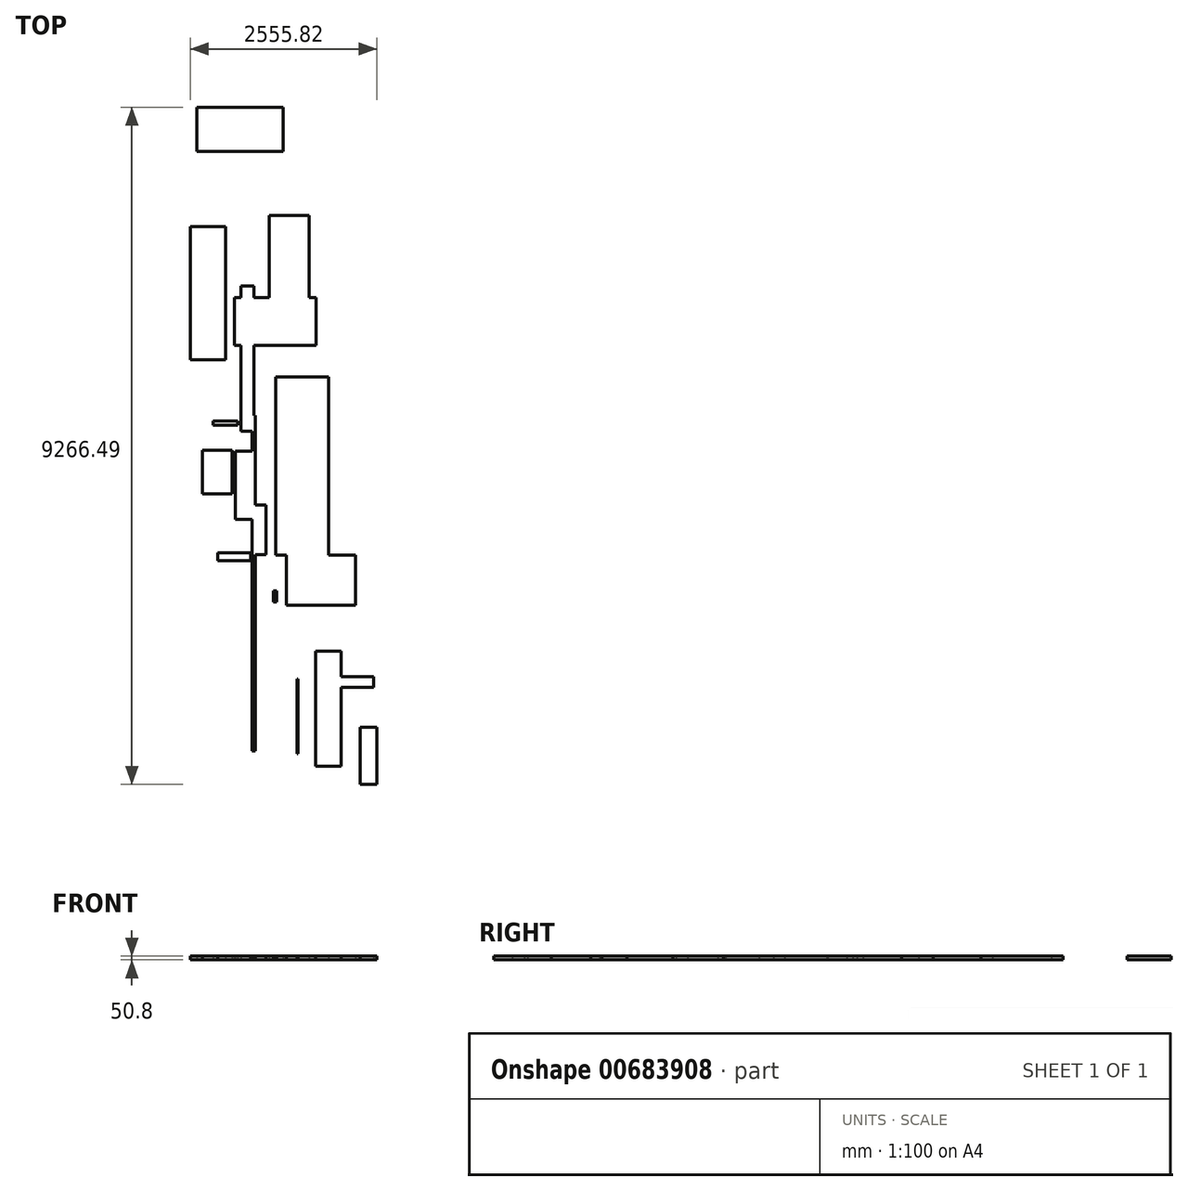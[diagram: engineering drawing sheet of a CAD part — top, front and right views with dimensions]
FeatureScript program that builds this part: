
annotation { "Feature Type Name" : "Feature", "Feature Type Description" : "" }
export const myFeature = defineFeature(function(context is Context, id is Id, definition is map)
    precondition{}
    {
        {
            var Q0;
            Q0=qCreatedBy(makeId("Top.planeOp"),FACE);
            var sketch = newSketch(context, id + "F0", { "sketchPlane" : qUnion([Q0])});
            skLineSegment(sketch, "E0.bottom", {"start": v(975.33, -2927.2) * mm, "end": v(1019.57, -2927.2) * mm});
            skLineSegment(sketch, "E0.top", {"start": v(975.33, -3083.63) * mm, "end": v(1019.57, -3083.63) * mm});
            skLineSegment(sketch, "E0.left", {"start": v(975.33, -2927.2) * mm, "end": v(975.33, -3083.63) * mm});
            skLineSegment(sketch, "E0.right", {"start": v(1019.57, -2927.2) * mm, "end": v(1019.57, -3083.63) * mm});
            skLineSegment(sketch, "E1.bottom", {"start": v(686.68, -1751.09) * mm, "end": v(872.32, -1751.09) * mm});
            skLineSegment(sketch, "E1.top", {"start": v(686.68, -2433.38) * mm, "end": v(872.32, -2433.38) * mm});
            skLineSegment(sketch, "E1.left", {"start": v(686.68, -1751.09) * mm, "end": v(686.68, -2433.38) * mm});
            skLineSegment(sketch, "E1.right", {"start": v(872.32, -1751.09) * mm, "end": v(872.32, -2433.38) * mm});
            skLineSegment(sketch, "E2.bottom", {"start": v(1010.2, 0) * mm, "end": v(1733.35, 0) * mm});
            skLineSegment(sketch, "E2.top", {"start": v(1010.2, -2436.83) * mm, "end": v(1733.35, -2436.83) * mm});
            skLineSegment(sketch, "E2.left", {"start": v(1010.2, 0) * mm, "end": v(1010.2, -2436.83) * mm});
            skLineSegment(sketch, "E2.right", {"start": v(1733.35, 0) * mm, "end": v(1733.35, -2436.83) * mm});
            skLineSegment(sketch, "E3.bottom", {"start": v(1109.4, 3085.25) * mm, "end": v(-73.1, 3085.25) * mm});
            skLineSegment(sketch, "E3.top", {"start": v(1109.4, 3687.99) * mm, "end": v(-73.1, 3687.99) * mm});
            skLineSegment(sketch, "E3.left", {"start": v(1109.4, 3085.25) * mm, "end": v(1109.4, 3687.99) * mm});
            skLineSegment(sketch, "E3.right", {"start": v(-73.1, 3085.25) * mm, "end": v(-73.1, 3687.99) * mm});
            skLineSegment(sketch, "E4.bottom", {"start": v(915.83, 1074.44) * mm, "end": v(1465.41, 1074.44) * mm});
            skLineSegment(sketch, "E4.top", {"start": v(915.83, 2210.7) * mm, "end": v(1465.41, 2210.7) * mm});
            skLineSegment(sketch, "E4.left", {"start": v(915.83, 1074.44) * mm, "end": v(915.83, 2210.7) * mm});
            skLineSegment(sketch, "E4.right", {"start": v(1465.41, 1074.44) * mm, "end": v(1465.41, 2210.7) * mm});
            skLineSegment(sketch, "E5.bottom", {"start": v(1563.04, 430.69) * mm, "end": v(444.98, 430.69) * mm});
            skLineSegment(sketch, "E5.top", {"start": v(1563.04, 1086.1) * mm, "end": v(444.98, 1086.1) * mm});
            skLineSegment(sketch, "E5.left", {"start": v(1563.04, 430.69) * mm, "end": v(1563.04, 1086.1) * mm});
            skLineSegment(sketch, "E5.right", {"start": v(444.98, 430.69) * mm, "end": v(444.98, 1086.1) * mm});
            skLineSegment(sketch, "E6.bottom", {"start": v(324.29, 236.13) * mm, "end": v(-161.62, 236.13) * mm});
            skLineSegment(sketch, "E6.top", {"start": v(324.29, 2053.76) * mm, "end": v(-161.62, 2053.76) * mm});
            skLineSegment(sketch, "E6.left", {"start": v(324.29, 236.13) * mm, "end": v(324.29, 2053.76) * mm});
            skLineSegment(sketch, "E6.right", {"start": v(-161.62, 236.13) * mm, "end": v(-161.62, 2053.76) * mm});
            skPoint(sketch, "E7.oppositeSnap0", {"position": v(686.68, -2092.23) * mm});
            skLineSegment(sketch, "E7.bottom", {"start": v(725.92, -5117.83) * mm, "end": v(686.68, -5117.83) * mm});
            skLineSegment(sketch, "E7.top", {"start": v(725.92, -526.4) * mm, "end": v(686.68, -526.4) * mm});
            skLineSegment(sketch, "E7.left", {"start": v(725.92, -5117.83) * mm, "end": v(725.92, -526.4) * mm});
            skLineSegment(sketch, "E7.right", {"start": v(686.68, -5117.83) * mm, "end": v(686.68, -526.4) * mm});
            skLineSegment(sketch, "E8.bottom", {"start": v(490.14, -662.8) * mm, "end": v(152.2, -662.8) * mm});
            skLineSegment(sketch, "E8.top", {"start": v(490.14, -607.24) * mm, "end": v(152.2, -607.24) * mm});
            skLineSegment(sketch, "E8.left", {"start": v(490.14, -662.8) * mm, "end": v(490.14, -607.24) * mm});
            skLineSegment(sketch, "E8.right", {"start": v(152.2, -662.8) * mm, "end": v(152.2, -607.24) * mm});
            skLineSegment(sketch, "E9.bottom", {"start": v(7.74, -1600.43) * mm, "end": v(412.88, -1600.43) * mm});
            skLineSegment(sketch, "E9.top", {"start": v(7.74, -1006.37) * mm, "end": v(412.88, -1006.37) * mm});
            skLineSegment(sketch, "E9.left", {"start": v(7.74, -1600.43) * mm, "end": v(7.74, -1006.37) * mm});
            skLineSegment(sketch, "E9.right", {"start": v(412.88, -1600.43) * mm, "end": v(412.88, -1006.37) * mm});
            skLineSegment(sketch, "E10.bottom", {"start": v(709.22, -1020.02) * mm, "end": v(455.88, -1020.02) * mm});
            skLineSegment(sketch, "E10.top", {"start": v(709.22, -1950.48) * mm, "end": v(455.88, -1950.48) * mm});
            skLineSegment(sketch, "E10.left", {"start": v(709.22, -1020.02) * mm, "end": v(709.22, -1950.48) * mm});
            skLineSegment(sketch, "E10.right", {"start": v(455.88, -1020.02) * mm, "end": v(455.88, -1950.48) * mm});
            skLineSegment(sketch, "E11.bottom", {"start": v(217.47, -2407.47) * mm, "end": v(663.15, -2407.47) * mm});
            skLineSegment(sketch, "E11.top", {"start": v(217.47, -2513.41) * mm, "end": v(663.15, -2513.41) * mm});
            skLineSegment(sketch, "E11.left", {"start": v(217.47, -2407.47) * mm, "end": v(217.47, -2513.41) * mm});
            skLineSegment(sketch, "E11.right", {"start": v(663.15, -2407.47) * mm, "end": v(663.15, -2513.41) * mm});
            skLineSegment(sketch, "E12.bottom", {"start": v(707.04, 1243.74) * mm, "end": v(532.7, 1243.74) * mm});
            skLineSegment(sketch, "E12.top", {"start": v(707.04, -745.15) * mm, "end": v(532.7, -745.15) * mm});
            skLineSegment(sketch, "E12.left", {"start": v(707.04, 1243.74) * mm, "end": v(707.04, -745.15) * mm});
            skLineSegment(sketch, "E12.right", {"start": v(532.7, 1243.74) * mm, "end": v(532.7, -745.15) * mm});
            skLineSegment(sketch, "E13.bottom", {"start": v(2394.2, -5578.5) * mm, "end": v(2161.19, -5578.5) * mm});
            skLineSegment(sketch, "E13.top", {"start": v(2394.2, -4794.63) * mm, "end": v(2161.19, -4794.63) * mm});
            skLineSegment(sketch, "E13.left", {"start": v(2394.2, -5578.5) * mm, "end": v(2394.2, -4794.63) * mm});
            skLineSegment(sketch, "E13.right", {"start": v(2161.19, -5578.5) * mm, "end": v(2161.19, -4794.63) * mm});
            skLineSegment(sketch, "E14.bottom", {"start": v(1902.45, -5327.25) * mm, "end": v(1553.8, -5327.25) * mm});
            skLineSegment(sketch, "E14.top", {"start": v(1902.45, -3754.76) * mm, "end": v(1553.8, -3754.76) * mm});
            skLineSegment(sketch, "E14.left", {"start": v(1902.45, -5327.25) * mm, "end": v(1902.45, -3754.76) * mm});
            skLineSegment(sketch, "E14.right", {"start": v(1553.8, -5327.25) * mm, "end": v(1553.8, -3754.76) * mm});
            skLineSegment(sketch, "E15.bottom", {"start": v(1313.08, -5158.48) * mm, "end": v(1299.9, -5158.48) * mm});
            skLineSegment(sketch, "E15.top", {"start": v(1313.08, -4134.75) * mm, "end": v(1299.9, -4134.75) * mm});
            skLineSegment(sketch, "E15.left", {"start": v(1313.08, -5158.48) * mm, "end": v(1313.08, -4134.75) * mm});
            skLineSegment(sketch, "E15.right", {"start": v(1299.9, -5158.48) * mm, "end": v(1299.9, -4134.75) * mm});
            skLineSegment(sketch, "E16.bottom", {"start": v(1696.29, -4251.25) * mm, "end": v(2346.64, -4251.25) * mm});
            skLineSegment(sketch, "E16.top", {"start": v(1696.29, -4100.28) * mm, "end": v(2346.64, -4100.28) * mm});
            skLineSegment(sketch, "E16.left", {"start": v(1696.29, -4251.25) * mm, "end": v(1696.29, -4100.28) * mm});
            skLineSegment(sketch, "E16.right", {"start": v(2346.64, -4251.25) * mm, "end": v(2346.64, -4100.28) * mm});
            skLineSegment(sketch, "E17.bottom", {"start": v(2098.27, -3126.85) * mm, "end": v(1156.3, -3126.85) * mm});
            skLineSegment(sketch, "E17.top", {"start": v(2098.27, -2436.83) * mm, "end": v(1156.3, -2436.83) * mm});
            skLineSegment(sketch, "E17.left", {"start": v(2098.27, -3126.85) * mm, "end": v(2098.27, -2436.83) * mm});
            skLineSegment(sketch, "E17.right", {"start": v(1156.3, -3126.85) * mm, "end": v(1156.3, -2436.83) * mm});
            skSolve(sketch);
        }
        {
            var Q0;
            Q0 = qSketchRegion(id + "F0", true);
            extrude(context, id + "F1", {"entities" : qUnion([Q0]), "depth" : 25.4 * mm, "offsetDistance" : 25.4 * mm, "hasSecondDirection" : true, "secondDirectionOppositeDirection" : true, "secondDirectionDepth" : 25.4 * mm});
        }
    });
